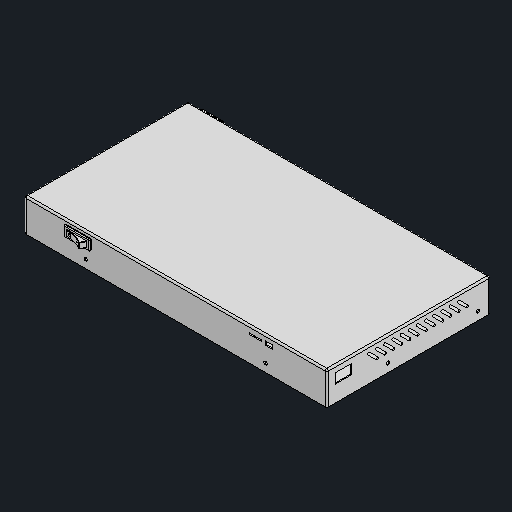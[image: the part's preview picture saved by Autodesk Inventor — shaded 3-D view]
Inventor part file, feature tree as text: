
AUTODESK INVENTOR PART (.ipt)
format: ipt  version: 2024.2 (Build 282272000, 272)  size: 707,072 bytes
history: native  units: mm
features: other x15, chamfer x1
ambient origin geometry x8: Origin, YZ Plane, XZ Plane, XY Plane, X Axis, Y Axis, Z Axis, Center Point
bodies: Body1 (feature_tree), Body2 (feature_tree), Body3 (feature_tree), Body4 (feature_tree), Body5 (feature_tree), Body6 (feature_tree), Body7 (feature_tree), Body8 (feature_tree)
feature tree (16):
  other  "솔리드1"
  other  "솔리드2"
  other  "솔리드3"
  other  "솔리드4"
  other  "솔리드5"
  other  "솔리드6"
  other  "솔리드7"
  other  "솔리드8"
  other  "Wrap2"
  other  "Cut-Extrude6[2]"
  other  "Cut-Extrude6[3]"
  chamfer  "Chamfer2"  [1 undecoded]
  other  "Boss-Extrude13"
  other  "Cut-Extrude9"
  other  "Boss-Extrude17"
  other  "Cut-Extrude11"
note: 1 required parameter value undecoded (feature->parameter linkage not recoverable at this tier; creation-order binding heuristic only, values carry confidence <= 0.55)
